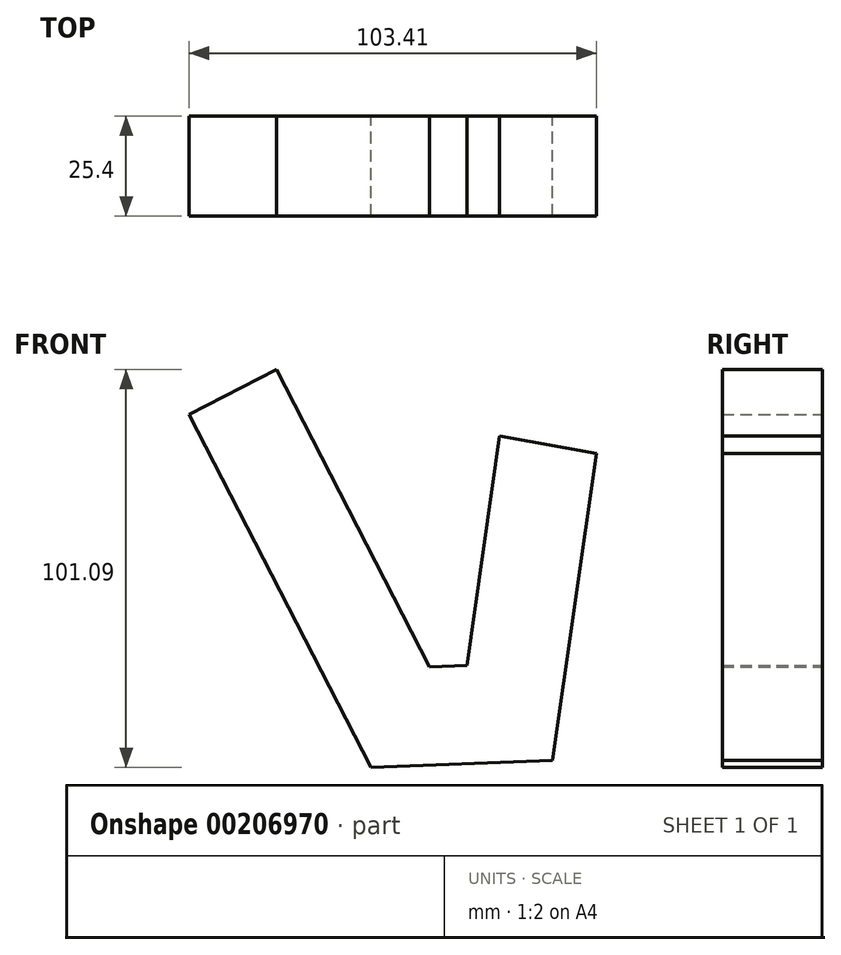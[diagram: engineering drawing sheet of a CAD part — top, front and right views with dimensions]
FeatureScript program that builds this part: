
annotation { "Feature Type Name" : "Feature", "Feature Type Description" : "" }
export const myFeature = defineFeature(function(context is Context, id is Id, definition is map)
    precondition{}
    {
        {
            var Q0;
            Q0=qCreatedBy(makeId("Front.planeOp"),FACE);
            var sketch = newSketch(context, id + "F0", { "sketchPlane" : qUnion([Q0])});
            skLineSegment(sketch, "E0", {"start": v(-46.17, 68.8) * mm, "end": v(0, -20.84) * mm});
            skLineSegment(sketch, "E1", {"start": v(46.17, -19.05) * mm, "end": v(0, -20.84) * mm});
            skLineSegment(sketch, "E2", {"start": v(46.17, -19.05) * mm, "end": v(57.24, 58.92) * mm});
            skLineSegment(sketch, "E3.0", {"start": v(24.35, 5.12) * mm, "end": v(32.63, 63.36) * mm});
            skLineSegment(sketch, "E3.1", {"start": v(24.35, 5.12) * mm, "end": v(14.94, 4.75) * mm});
            skLineSegment(sketch, "E3.2", {"start": v(-23.94, 80.25) * mm, "end": v(14.94, 4.75) * mm});
            skLineSegment(sketch, "E4", {"start": v(-46.17, 68.8) * mm, "end": v(-23.94, 80.25) * mm});
            skLineSegment(sketch, "E5", {"start": v(32.63, 63.36) * mm, "end": v(57.24, 58.92) * mm});
            skSolve(sketch);
        }
        {
            var Q0;
            Q0=makeQuery(id+"F0.imprint","IMPRINT",FACE,{"disambiguationData":[TD([[makeQuery(id+"F0.imprint","IMPRINT",EDGE,{"derivedFrom":sQuery(id+"F0.wireOp",EDGE,"E0")}),1.0]])]});
            extrude(context, id + "F1", {"entities" : qUnion([Q0]), "depth" : 25.4 * mm});
        }
    });
